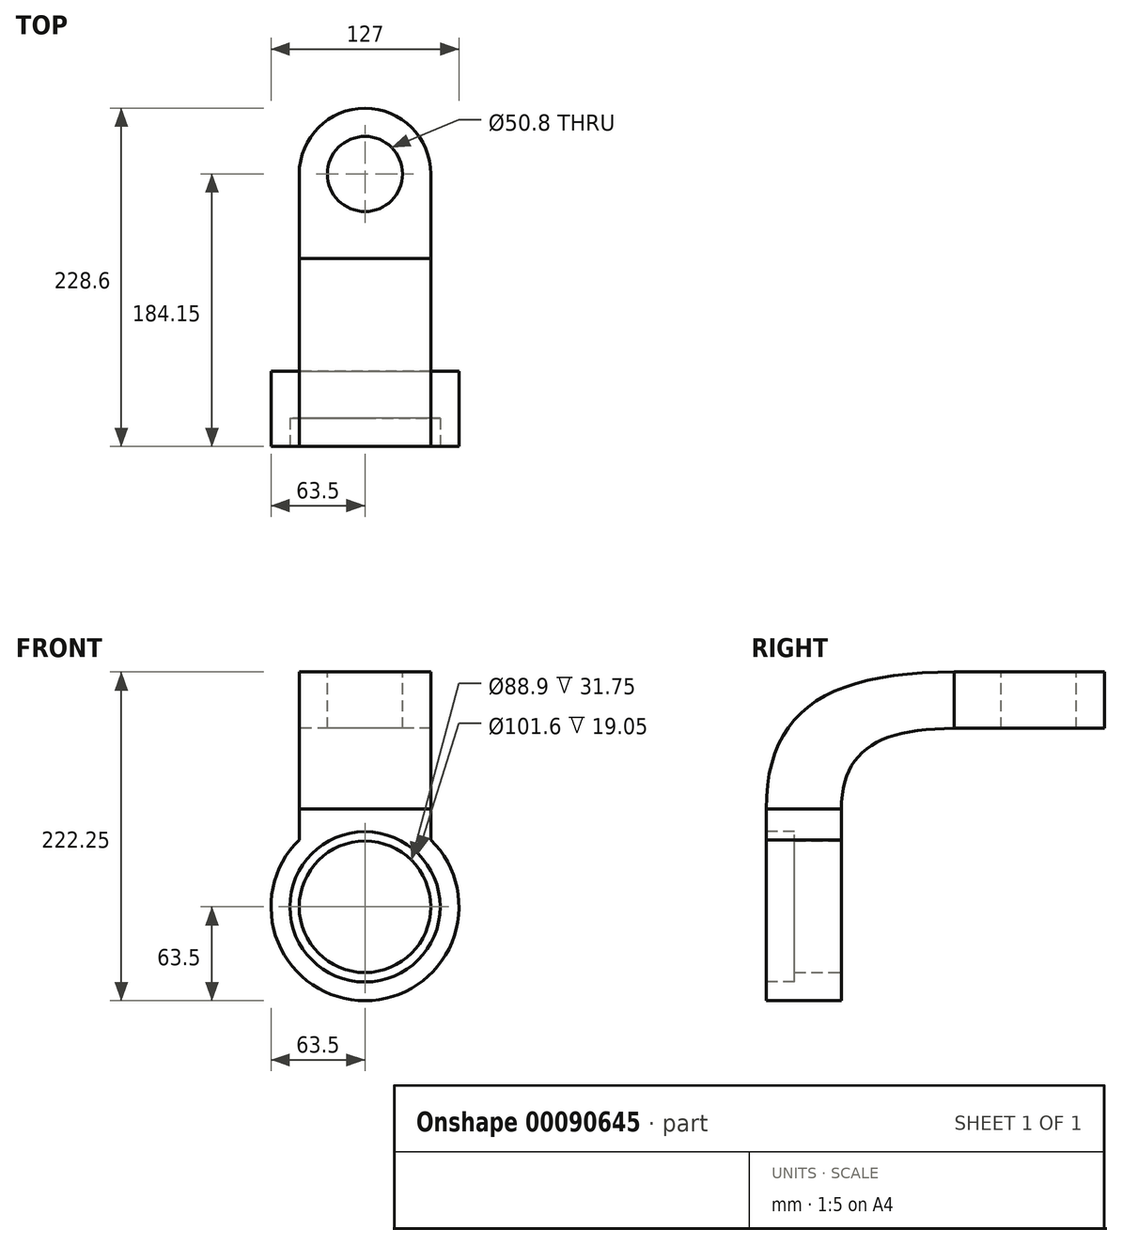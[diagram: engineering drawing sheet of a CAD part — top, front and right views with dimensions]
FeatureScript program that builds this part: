
annotation { "Feature Type Name" : "Feature", "Feature Type Description" : "" }
export const myFeature = defineFeature(function(context is Context, id is Id, definition is map)
    precondition{}
    {
        {
            var Q0;
            Q0=qCreatedBy(makeId("Front.planeOp"),FACE);
            var sketch = newSketch(context, id + "F0", { "sketchPlane" : qUnion([Q0])});
            skCircle(sketch, "E0", {"center": v(0, 0) * mm, "radius": 63.5 * mm});
            skCircle(sketch, "E1", {"center": v(0, 0) * mm, "radius": 44.45 * mm});
            skSolve(sketch);
        }
        {
            var Q0;
            Q0 = qSketchRegion(id + "F0", true);
            extrude(context, id + "F1", {"entities" : qUnion([Q0]), "endBound" : BoundingType.SYMMETRIC, "depth" : 50.8 * mm});
        }
        {
            var Q0;
            Q0=makeQuery(id+"F1.opExtrude","CAP_FACE",FACE,{"disambiguationData":[OSD([sQuery(id+"F0.wireOp",EDGE,"E0"),sQuery(id+"F0.wireOp",EDGE,"E1")])],"isStart":false});
            var sketch = newSketch(context, id + "F2", { "sketchPlane" : qUnion([Q0])});
            skCircle(sketch, "E2", {"center": v(0, 0) * mm, "radius": 50.8 * mm});
            skCircle(sketch, "E3.0", {"center": v(0, 0) * mm, "radius": 44.45 * mm});
            skSolve(sketch);
        }
        {
            var Q0;
            Q0=makeQuery(id+"F2.imprint","IMPRINT",FACE,{"disambiguationData":[TD([[makeQuery(id+"F2.imprint","IMPRINT",EDGE,{"derivedFrom":sQuery(id+"F2.wireOp",EDGE,"E2")}),1.0]])]});
            extrude(context, id + "F3", {"entities" : qUnion([Q0]), "operationType" : NewBodyOperationType.REMOVE, "oppositeDirection" : true, "depth" : 19.05 * mm});
        }
        {
            var Q0;
            Q0=qCreatedBy(makeId("Top.planeOp"),FACE);
            cPlane(context, id + "F4", {"entities" : qUnion([Q0]), "cplaneType" : CPlaneType.OFFSET, "offset" : 63.5 * mm, "width" : 152.4 * mm, "height" : 152.4 * mm});
        }
        {
            var Q0;
            Q0=qCreatedBy(id+"F4.planeOp",FACE);
            var sketch = newSketch(context, id + "F5", { "sketchPlane" : qUnion([Q0])});
            skLineSegment(sketch, "E4.bottom", {"start": v(44.45, 25.4) * mm, "end": v(-44.45, 25.4) * mm});
            skLineSegment(sketch, "E4.top", {"start": v(44.45, -25.4) * mm, "end": v(-44.45, -25.4) * mm});
            skLineSegment(sketch, "E4.left", {"start": v(44.45, 25.4) * mm, "end": v(44.45, -25.4) * mm});
            skLineSegment(sketch, "E4.right", {"start": v(-44.45, 25.4) * mm, "end": v(-44.45, -25.4) * mm});
            skPoint(sketch, "E4.middle", {"position": v(0, 0) * mm});
            skLineSegment(sketch, "E5", {"start": v(0, 25.4) * mm, "end": v(0, -25.4) * mm, "construction": true});
            skSolve(sketch);
        }
        {
            var Q0;
            Q0=makeQuery(id+"F1.opExtrude","CAP_FACE",FACE,{"disambiguationData":[OSD([sQuery(id+"F0.wireOp",EDGE,"E0"),sQuery(id+"F0.wireOp",EDGE,"E1")])],"isStart":true});
            cPlane(context, id + "F6", {"entities" : qUnion([Q0]), "cplaneType" : CPlaneType.OFFSET, "offset" : 76.2 * mm, "width" : 152.4 * mm, "height" : 152.4 * mm});
        }
        {
            var Q0;
            Q0=qCreatedBy(id+"F6.planeOp",FACE);
            var sketch = newSketch(context, id + "F7", { "sketchPlane" : qUnion([Q0])});
            skLineSegment(sketch, "E6.bottom", {"start": v(-44.45, 158.75) * mm, "end": v(44.45, 158.75) * mm});
            skLineSegment(sketch, "E6.top", {"start": v(-44.45, 120.65) * mm, "end": v(44.45, 120.65) * mm});
            skLineSegment(sketch, "E6.left", {"start": v(-44.45, 158.75) * mm, "end": v(-44.45, 120.65) * mm});
            skLineSegment(sketch, "E6.right", {"start": v(44.45, 158.75) * mm, "end": v(44.45, 120.65) * mm});
            skPoint(sketch, "E6.middle", {"position": v(0, 139.7) * mm});
            skLineSegment(sketch, "E7.0", {"start": v(-44.45, 63.5) * mm, "end": v(44.45, 63.5) * mm, "construction": true});
            skLineSegment(sketch, "E8", {"start": v(0, 0) * mm, "end": v(0, 139.7) * mm, "construction": true});
            skSolve(sketch);
        }
        {
            var Q0;
            Q0=makeQuery(id+"F7.imprint","IMPRINT",FACE,{"disambiguationData":[TD([[makeQuery(id+"F7.imprint","IMPRINT",EDGE,{"derivedFrom":sQuery(id+"F7.wireOp",EDGE,"E6.bottom")}),-1.0]])]});
            extrude(context, id + "F8", {"entities" : qUnion([Q0]), "depth" : 101.6 * mm});
        }
        {
            var Q0;
            Q0=makeQuery(id+"F8.opExtrude","SWEPT_FACE",FACE,{"disambiguationData":[OSD([sQuery(id+"F7.wireOp",EDGE,"E6.bottom")])]});
            var sketch = newSketch(context, id + "F9", { "sketchPlane" : qUnion([Q0])});
            skCircle(sketch, "E9", {"center": v(0, 158.75) * mm, "radius": 44.45 * mm});
            skCircle(sketch, "E10", {"center": v(0, 158.75) * mm, "radius": 25.4 * mm});
            skSolve(sketch);
        }
        {
            var Q0;
            {var subQ0=sQuery(id+"F9.wireOp",EDGE,"E9");var subQ1=sQuery(id+"F7.wireOp",EDGE,"E6.bottom");var subQ2=makeQuery(id+"F8.opExtrude","CAP_EDGE",EDGE,{"disambiguationData":[OSD([subQ1])],"isStart":false});var subQ3=makeQuery(id+"F9.imprint","INTERSECT",VERTEX,{"derivedFrom":[subQ2,subQ0]});Q0=makeQuery(id+"F9.imprint","IMPRINT",FACE,{"disambiguationData":[TD([[makeQuery(id+"F9.imprint","IMPRINT",EDGE,{"disambiguationData":[TD([[subQ3,1.0]])],"derivedFrom":subQ0}),-1.0]])]});}
            var Q1;
            {var subQ0=sQuery(id+"F9.wireOp",EDGE,"E9");var subQ1=sQuery(id+"F7.wireOp",EDGE,"E6.bottom");var subQ2=makeQuery(id+"F8.opExtrude","CAP_EDGE",EDGE,{"disambiguationData":[OSD([subQ1])],"isStart":false});var subQ3=makeQuery(id+"F9.imprint","INTERSECT",VERTEX,{"derivedFrom":[subQ2,subQ0]});Q1=makeQuery(id+"F9.imprint","IMPRINT",FACE,{"disambiguationData":[TD([[makeQuery(id+"F9.imprint","IMPRINT",EDGE,{"disambiguationData":[TD([[subQ3,-1.0]])],"derivedFrom":subQ0}),-1.0]])]});}
            var Q2;
            Q2=makeQuery(id+"F9.imprint","IMPRINT",FACE,{"disambiguationData":[TD([[makeQuery(id+"F9.imprint","IMPRINT",EDGE,{"derivedFrom":sQuery(id+"F9.wireOp",EDGE,"E10")}),1.0]])]});
            var Q3;
            Q3=makeQuery(id+"F8.opExtrude","SWEPT_FACE",FACE,{"disambiguationData":[OSD([sQuery(id+"F7.wireOp",EDGE,"E6.top")])]});
            extrude(context, id + "F10", {"entities" : qUnion([Q0, Q1, Q2]), "operationType" : NewBodyOperationType.REMOVE, "endBound" : BoundingType.UP_TO_SURFACE, "oppositeDirection" : true, "endBoundEntityFace" : qUnion([Q3]), "depth" : 25.4 * mm});
        }
        {
            var Q0;
            Q0=makeQuery(id+"F5.imprint","IMPRINT",FACE,{"disambiguationData":[TD([[makeQuery(id+"F5.imprint","IMPRINT",EDGE,{"derivedFrom":sQuery(id+"F5.wireOp",EDGE,"E4.bottom")}),1.0]])]});
            var Q1;
            Q1=makeQuery(id+"F1.opExtrude","SWEPT_FACE",FACE,{"disambiguationData":[OSD([sQuery(id+"F0.wireOp",EDGE,"E0")])]});
            var Q2;
            Q2=makeQuery(id+"F1.opExtrude","SWEPT_BODY",BODY,{"disambiguationData":[OSD([sQuery(id+"F0.wireOp",EDGE,"E0"),sQuery(id+"F0.wireOp",EDGE,"E1")])]});
            extrude(context, id + "F11", {"entities" : qUnion([Q0]), "operationType" : NewBodyOperationType.ADD, "endBound" : BoundingType.UP_TO_BODY, "oppositeDirection" : true, "endBoundEntityFace" : qUnion([Q1]), "endBoundEntityBody" : qUnion([Q2]), "depth" : 25.4 * mm, "hasSecondDirection" : true, "secondDirectionOppositeDirection" : false, "secondDirectionDepth" : 2.54 * mm});
        }
        {
            var Q0;
            Q0=makeQuery(id+"F11.opExtrude","CAP_FACE",FACE,{"disambiguationData":[OSD([sQuery(id+"F5.wireOp",EDGE,"E4.bottom"),sQuery(id+"F5.wireOp",EDGE,"E4.top"),sQuery(id+"F5.wireOp",EDGE,"E4.left"),sQuery(id+"F5.wireOp",EDGE,"E4.right")])],"isStart":true});
            var Q1;
            Q1=makeQuery(id+"F7.imprint","IMPRINT",FACE,{"disambiguationData":[TD([[makeQuery(id+"F7.imprint","IMPRINT",EDGE,{"derivedFrom":sQuery(id+"F7.wireOp",EDGE,"E6.bottom")}),-1.0]])]});
            loft(context, id + "F12", {"startCondition" : LoftEndDerivativeType.NORMAL_TO_PROFILE, "startMagnitude" : 2, "endCondition" : LoftEndDerivativeType.NORMAL_TO_PROFILE, "endMagnitude" : 2, "sheetProfilesArray" : [{ "sheetProfileEntities" : qUnion([Q0]) }, { "sheetProfileEntities" : qUnion([Q1]) }]});
        }
        {
            var Q0;
            Q0=qCreatedBy(makeId("Top.planeOp"),FACE);
            cPlane(context, id + "F13", {"entities" : qUnion([Q0]), "cplaneType" : CPlaneType.OFFSET, "offset" : 63.5 * mm, "oppositeDirection" : true, "width" : 152.4 * mm, "height" : 152.4 * mm});
        }
    });
